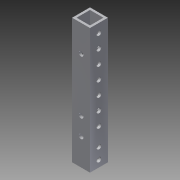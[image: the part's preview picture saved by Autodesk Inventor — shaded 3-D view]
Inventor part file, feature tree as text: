
AUTODESK INVENTOR PART (.ipt)
format: ipt  version: 2013 (Build 170138000, 138)  size: 145,408 bytes
history: native  units: in
note: dims shown in document units (in); Inventor stores cm internally (conversion verified against a paired STEP export)
features: extrude x4, sketch x4, reference x2
ambient origin geometry x8: Origin, YZ Plane, XZ Plane, XY Plane, X Axis, Y Axis, Z Axis, Center Point
bodies: Solid1 (feature_tree)
feature tree (10):
  extrude  "Extrusion1"  Depth=1.0in
  extrude  "Extrusion2"  Depth=7.0in TaperAngle=0.0deg
  extrude  "Extrusion3"  Depth=0.26in
  extrude  "Extrusion4"  Depth=4.25in
  sketch  "Sketch1"  dims[d0=1.0in d1=1.0in]
  sketch  "Sketch2"  dims[d2=0.125in d3=7.0in d4=0.0in]
  reference  "Reference1"
  reference  "Reference2"
  sketch  "Sketch3"  dims[d7=1.0in d8=0.0in d17=0.26in]
  sketch  "Sketch4"  dims[d18=0.26in d19=4.25in d20=0.26in d21=0.5in d22=0.5in d23=0.26in d25=1.0in d26=2.3622in d28=0.75in d29=0.3937in d31=1.0in d33=1.0in d34=0.0in d35=1.5in d36=0.26in d37=1.9685in d39=1.0in d40=0.3937in d42=1.0in d44=1.0in d45=0.0in]
